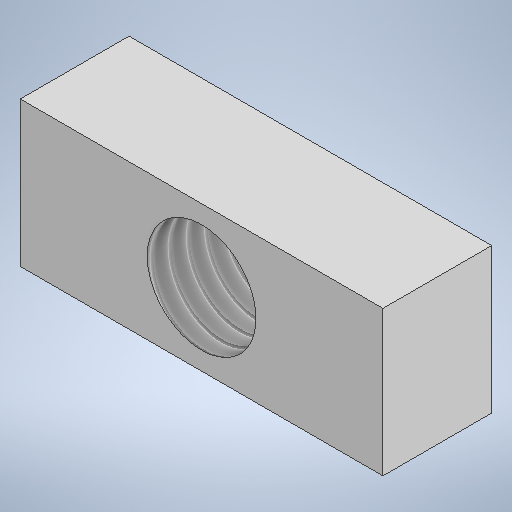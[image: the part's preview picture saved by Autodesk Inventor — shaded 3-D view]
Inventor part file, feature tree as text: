
AUTODESK INVENTOR PART (.ipt)
format: ipt  version: 2025.1 (Build 291241000, 241)  size: 208,896 bytes
history: native  units: mm
features: extrude x2, sketch x2, thread x1
ambient origin geometry x8: Origin, YZ Plane, XZ Plane, XY Plane, X Axis, Y Axis, Z Axis, Center Point
bodies: Solid1 (feature_tree)
feature tree (5):
  extrude  "Extrusion1"  Depth=10.0mm
  extrude  "Extrusion2"  Depth=3.0mm
  thread  "Thread1"  [1 undecoded]
  sketch  "Sketch1"  dims[d0=3.0mm d1=10.0mm]
  sketch  "Sketch2"  dims[d2=4.0mm d3=0.0mm d4=3.0mm d5=4.0mm d6=0.0mm d7=35.9mm d8=0.0mm]
note: 1 required parameter value undecoded (feature->parameter linkage not recoverable at this tier; creation-order binding heuristic only, values carry confidence <= 0.55)
